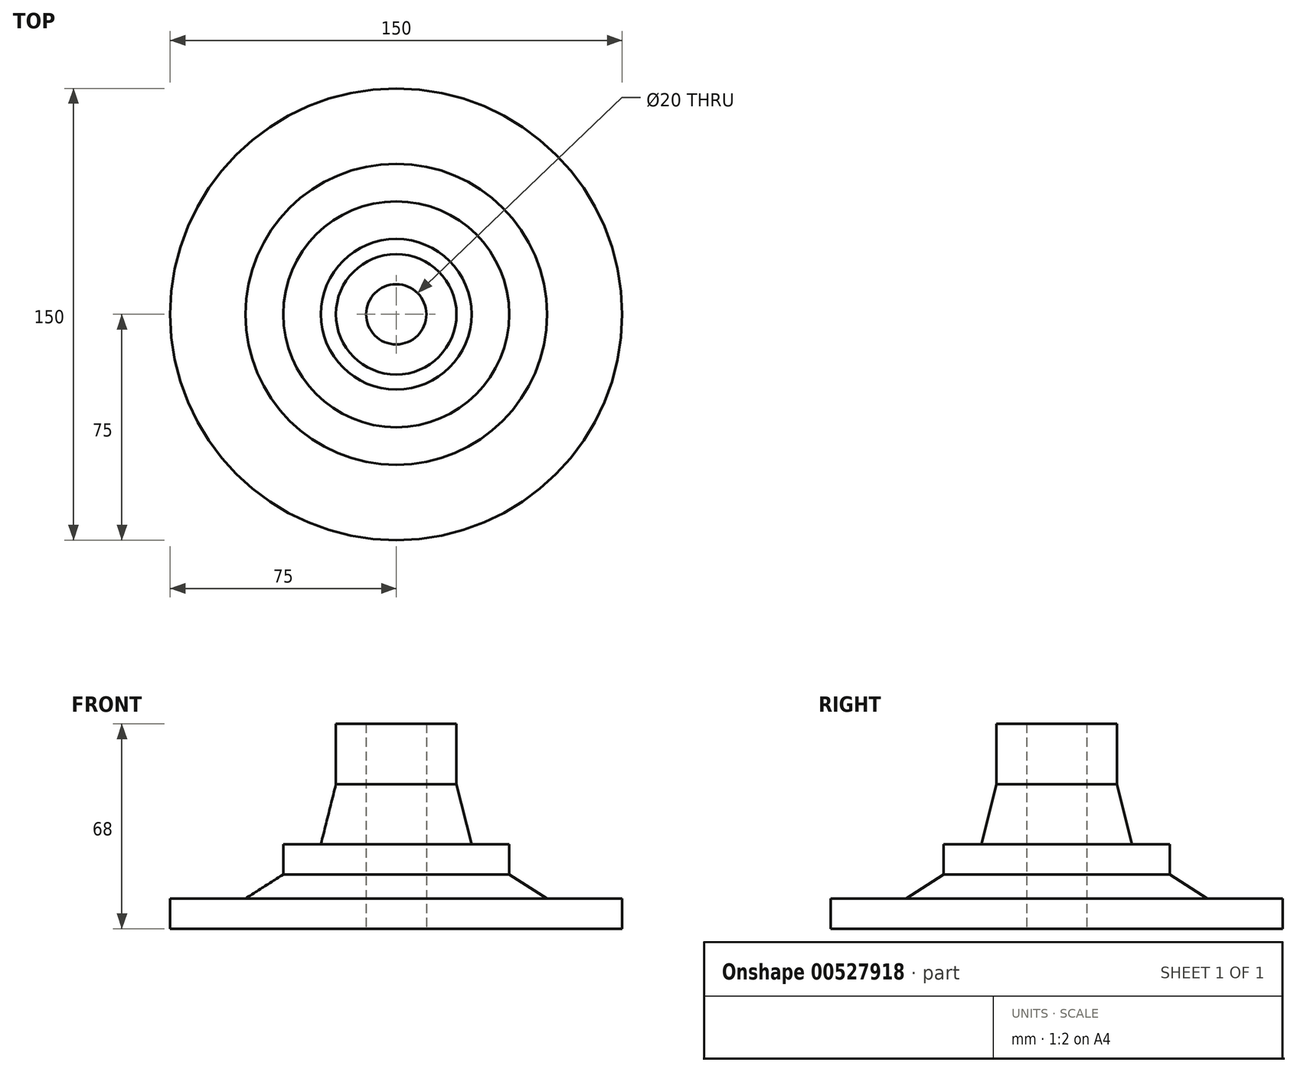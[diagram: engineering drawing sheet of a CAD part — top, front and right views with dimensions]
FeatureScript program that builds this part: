
annotation { "Feature Type Name" : "Feature", "Feature Type Description" : "" }
export const myFeature = defineFeature(function(context is Context, id is Id, definition is map)
    precondition{}
    {
        {
            var Q0;
            Q0=qCreatedBy(makeId("Front.planeOp"),FACE);
            var sketch = newSketch(context, id + "F0", { "sketchPlane" : qUnion([Q0])});
            skLineSegment(sketch, "E0", {"start": v(0, 0) * mm, "end": v(0, 73.16) * mm});
            skLineSegment(sketch, "E1", {"start": v(-10, 0) * mm, "end": v(-10, 68) * mm});
            skLineSegment(sketch, "E2", {"start": v(-10, 68) * mm, "end": v(-20, 68) * mm});
            skLineSegment(sketch, "E3", {"start": v(-20, 68) * mm, "end": v(-20, 48) * mm});
            skLineSegment(sketch, "E4", {"start": v(-20, 48) * mm, "end": v(-25, 28) * mm});
            skLineSegment(sketch, "E5", {"start": v(-25, 28) * mm, "end": v(-37.5, 28) * mm});
            skLineSegment(sketch, "E6", {"start": v(-37.5, 28) * mm, "end": v(-37.5, 18) * mm});
            skLineSegment(sketch, "E7", {"start": v(-37.5, 18) * mm, "end": v(-50, 10) * mm});
            skLineSegment(sketch, "E8", {"start": v(-50, 10) * mm, "end": v(-75, 10) * mm});
            skLineSegment(sketch, "E9", {"start": v(-75, 10) * mm, "end": v(-75, 0) * mm});
            skLineSegment(sketch, "E10", {"start": v(-75, 0) * mm, "end": v(-10, 0) * mm});
            skSolve(sketch);
        }
        {
            var Q0;
            Q0 = qSketchRegion(id + "F0", true);
            var Q1;
            Q1=sQuery(id+"F0.wireOp",EDGE,"E0");
            revolve(context, id + "F1", {"entities" : qUnion([Q0]), "axis" : qUnion([Q1]), "revolveType" : RevolveType.FULL});
        }
    });
